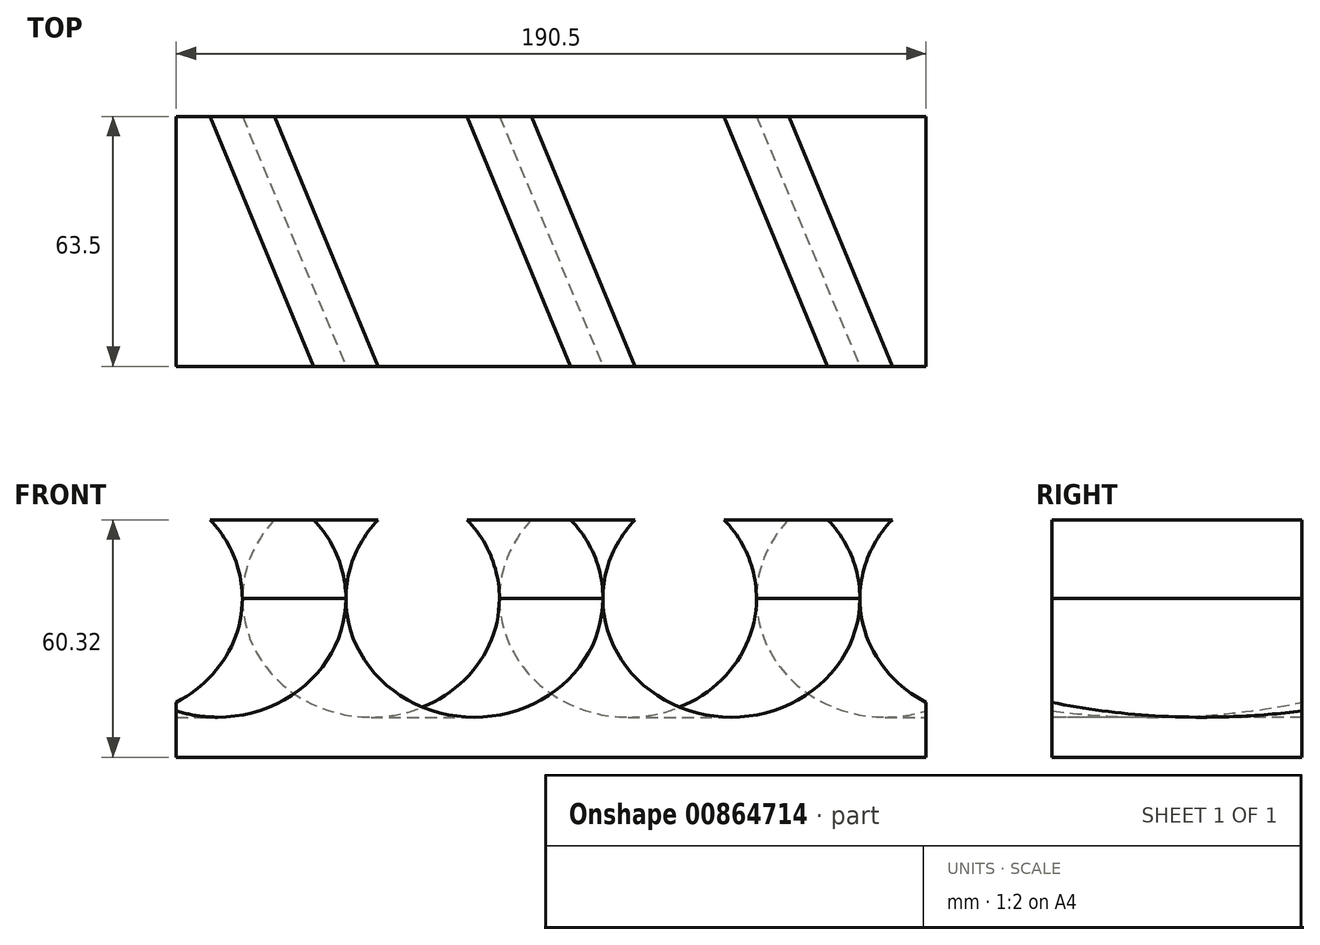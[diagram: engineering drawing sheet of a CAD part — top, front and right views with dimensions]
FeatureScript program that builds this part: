
annotation { "Feature Type Name" : "Feature", "Feature Type Description" : "" }
export const myFeature = defineFeature(function(context is Context, id is Id, definition is map)
    precondition{}
    {
        {
            var Q0;
            Q0=qCreatedBy(makeId("Front.planeOp"),FACE);
            var sketch = newSketch(context, id + "F0", { "sketchPlane" : qUnion([Q0])});
            skLineSegment(sketch, "E0.bottom", {"start": v(-95.25, 30.16) * mm, "end": v(95.25, 30.16) * mm});
            skLineSegment(sketch, "E0.top", {"start": v(-95.25, -30.16) * mm, "end": v(95.25, -30.16) * mm});
            skLineSegment(sketch, "E0.left", {"start": v(-95.25, 30.16) * mm, "end": v(-95.25, -30.16) * mm});
            skLineSegment(sketch, "E0.right", {"start": v(95.25, 30.16) * mm, "end": v(95.25, -30.16) * mm});
            skPoint(sketch, "E0.middle", {"position": v(0, 0) * mm});
            skSolve(sketch);
        }
        {
            var Q0;
            Q0=makeQuery(id+"F0.imprint","IMPRINT",FACE,{"disambiguationData":[TD([[makeQuery(id+"F0.imprint","IMPRINT",EDGE,{"derivedFrom":sQuery(id+"F0.wireOp",EDGE,"E0.bottom")}),-1.0]])]});
            extrude(context, id + "F1", {"entities" : qUnion([Q0]), "endBound" : BoundingType.SYMMETRIC, "depth" : 63.5 * mm, "offsetDistance" : 25.4 * mm});
        }
        {
            var Q0;
            Q0=qCreatedBy(makeId("Top.planeOp"),FACE);
            var sketch = newSketch(context, id + "F2", { "sketchPlane" : qUnion([Q0])});
            skLineSegment(sketch, "E1", {"start": v(92.84, 38.45) * mm, "end": v(-97.4, -40.35) * mm});
            skSolve(sketch);
        }
        {
            var Q0;
            Q0=sQuery(id+"F2.wireOp",EDGE,"E1");
            cPlane(context, id + "F3", {"entities" : qUnion([Q0]), "cplaneType" : CPlaneType.LINE_ANGLE, "offset" : 25.4 * mm, "angle" : 0 * degree, "width" : 152.4 * mm, "height" : 152.4 * mm});
        }
        {
            var Q0;
            Q0=qCreatedBy(id+"F3.planeOp",FACE);
            var sketch = newSketch(context, id + "F4", { "sketchPlane" : qUnion([Q0])});
            skCircle(sketch, "E2", {"center": v(-90.49, 10.16) * mm, "radius": 30.16 * mm});
            skCircle(sketch, "E3", {"center": v(-30.16, 10.16) * mm, "radius": 30.16 * mm});
            skCircle(sketch, "E4", {"center": v(30.16, 10.16) * mm, "radius": 30.16 * mm});
            skCircle(sketch, "E5", {"center": v(90.49, 10.16) * mm, "radius": 30.16 * mm});
            skSolve(sketch);
        }
        {
            var Q0;
            Q0=makeQuery(id+"F4.imprint","IMPRINT",FACE,{"disambiguationData":[TD([[makeQuery(id+"F4.imprint","IMPRINT",EDGE,{"derivedFrom":sQuery(id+"F4.wireOp",EDGE,"E2")}),1.0]])]});
            var Q1;
            {var subQ0=sQuery(id+"F4.wireOp",EDGE,"E3");var subQ1=makeQuery(id+"F4.imprint","INTERSECT",VERTEX,{"derivedFrom":[sQuery(id+"F4.wireOp",EDGE,"E2"),subQ0]});Q1=makeQuery(id+"F4.imprint","IMPRINT",FACE,{"disambiguationData":[TD([[makeQuery(id+"F4.imprint","IMPRINT",EDGE,{"disambiguationData":[TD([[subQ1,1.0]])],"derivedFrom":subQ0}),1.0]])]});}
            var Q2;
            {var subQ0=sQuery(id+"F4.wireOp",EDGE,"E4");var subQ1=makeQuery(id+"F4.imprint","INTERSECT",VERTEX,{"derivedFrom":[sQuery(id+"F4.wireOp",EDGE,"E3"),subQ0]});Q2=makeQuery(id+"F4.imprint","IMPRINT",FACE,{"disambiguationData":[TD([[makeQuery(id+"F4.imprint","IMPRINT",EDGE,{"disambiguationData":[TD([[subQ1,1.0]])],"derivedFrom":subQ0}),1.0]])]});}
            var Q3;
            Q3=makeQuery(id+"F4.imprint","IMPRINT",FACE,{"disambiguationData":[TD([[makeQuery(id+"F4.imprint","IMPRINT",EDGE,{"derivedFrom":sQuery(id+"F4.wireOp",EDGE,"E5")}),1.0]])]});
            extrude(context, id + "F5", {"entities" : qUnion([Q0, Q1, Q2, Q3]), "operationType" : NewBodyOperationType.REMOVE, "endBound" : BoundingType.SYMMETRIC, "oppositeDirection" : true, "depth" : 177.8 * mm, "offsetDistance" : 25.4 * mm});
        }
    });
